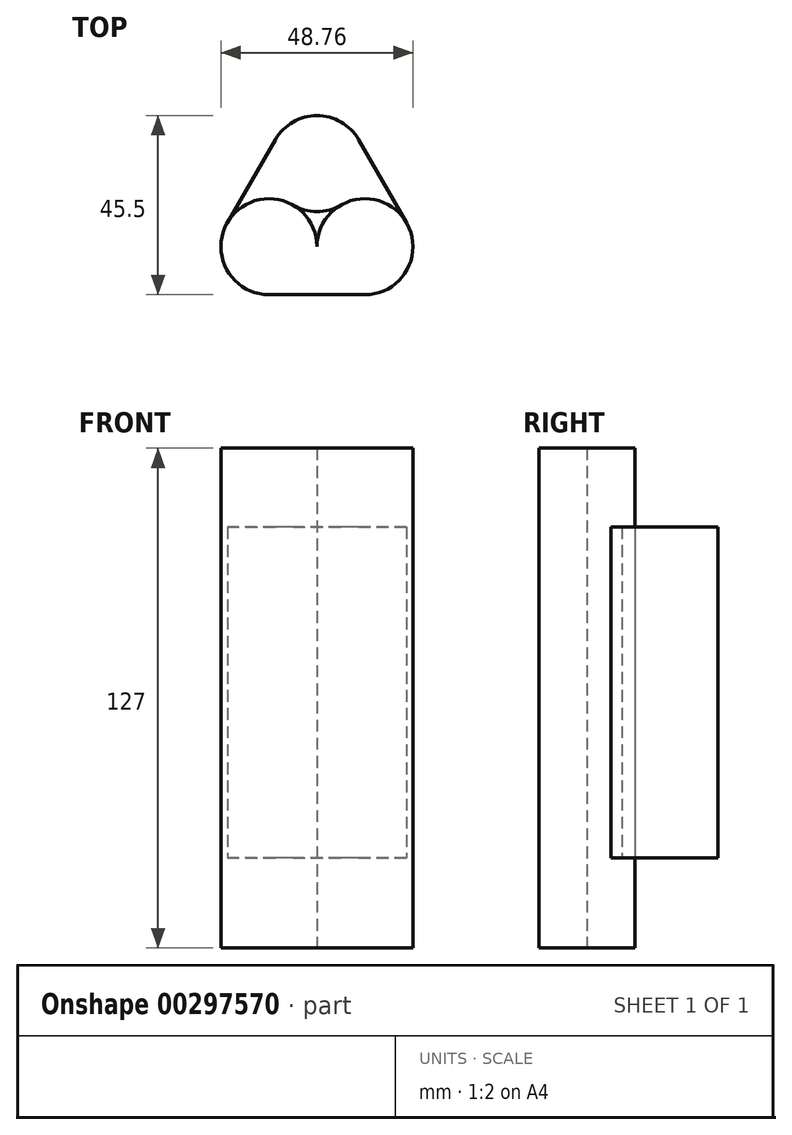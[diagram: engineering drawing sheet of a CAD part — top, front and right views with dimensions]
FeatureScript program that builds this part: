
annotation { "Feature Type Name" : "Feature", "Feature Type Description" : "" }
export const myFeature = defineFeature(function(context is Context, id is Id, definition is map)
    precondition{}
    {
        {
            var Q0;
            Q0=qCreatedBy(makeId("Top.planeOp"),FACE);
            var sketch = newSketch(context, id + "F0", { "sketchPlane" : qUnion([Q0])});
            skCircle(sketch, "E0", {"center": v(-12.2, 0) * mm, "radius": 12.2 * mm});
            skCircle(sketch, "E1", {"center": v(12.2, 0) * mm, "radius": 12.2 * mm});
            skCircle(sketch, "E2", {"center": v(0, 21.12) * mm, "radius": 12.2 * mm});
            skLineSegment(sketch, "E3", {"start": v(-12.2, -12.2) * mm, "end": v(12.2, -12.2) * mm});
            skLineSegment(sketch, "E4", {"start": v(-22.75, 6.1) * mm, "end": v(-10.56, 27.21) * mm});
            skLineSegment(sketch, "E5", {"start": v(10.56, 27.21) * mm, "end": v(22.75, 6.1) * mm});
            skSolve(sketch);
        }
        {
            var Q0;
            {var subQ0=sQuery(id+"F0.wireOp",EDGE,"E1");var subQ1=makeQuery(id+"F0.imprint","INTERSECT",VERTEX,{"derivedFrom":[sQuery(id+"F0.wireOp",EDGE,"E0"),subQ0]});Q0=makeQuery(id+"F0.imprint","IMPRINT",FACE,{"disambiguationData":[TD([[makeQuery(id+"F0.imprint","IMPRINT",EDGE,{"disambiguationData":[TD([[subQ1,1.0]])],"derivedFrom":subQ0}),1.0]])]});}
            var Q1;
            {var subQ0=sQuery(id+"F0.wireOp",EDGE,"E0");var subQ1=makeQuery(id+"F0.imprint","INTERSECT",VERTEX,{"derivedFrom":[subQ0,sQuery(id+"F0.wireOp",EDGE,"E1")]});Q1=makeQuery(id+"F0.imprint","IMPRINT",FACE,{"disambiguationData":[TD([[makeQuery(id+"F0.imprint","IMPRINT",EDGE,{"disambiguationData":[TD([[subQ1,-1.0]])],"derivedFrom":subQ0}),1.0]])]});}
            var Q2;
            {var subQ0=sQuery(id+"F0.wireOp",EDGE,"E3");Q2=makeQuery(id+"F0.imprint","IMPRINT",FACE,{"disambiguationData":[TD([[makeQuery(id+"F0.imprint","IMPRINT",EDGE,{"derivedFrom":subQ0}),1.0]])]});}
            extrude(context, id + "F1", {"entities" : qUnion([Q0, Q1, Q2]), "depth" : 127 * mm});
        }
        {
            var Q0;
            {var subQ0=sQuery(id+"F0.wireOp",EDGE,"E2");var subQ1=makeQuery(id+"F0.imprint","INTERSECT",VERTEX,{"derivedFrom":[subQ0,sQuery(id+"F0.wireOp",EDGE,"E4")]});Q0=makeQuery(id+"F0.imprint","IMPRINT",FACE,{"disambiguationData":[TD([[makeQuery(id+"F0.imprint","IMPRINT",EDGE,{"disambiguationData":[TD([[subQ1,1.0]])],"derivedFrom":subQ0}),1.0]])]});}
            var Q1;
            {var subQ0=sQuery(id+"F0.wireOp",EDGE,"E5");Q1=makeQuery(id+"F0.imprint","IMPRINT",FACE,{"disambiguationData":[TD([[makeQuery(id+"F0.imprint","IMPRINT",EDGE,{"derivedFrom":subQ0}),-1.0]])]});}
            var Q2;
            {var subQ0=sQuery(id+"F0.wireOp",EDGE,"E4");Q2=makeQuery(id+"F0.imprint","IMPRINT",FACE,{"disambiguationData":[TD([[makeQuery(id+"F0.imprint","IMPRINT",EDGE,{"derivedFrom":subQ0}),-1.0]])]});}
            extrude(context, id + "F2", {"entities" : qUnion([Q0, Q1, Q2]), "depth" : 106.93 * mm, "hasSecondDirection" : true, "secondDirectionOppositeDirection" : false, "secondDirectionDepth" : 22.86 * mm});
        }
    });
